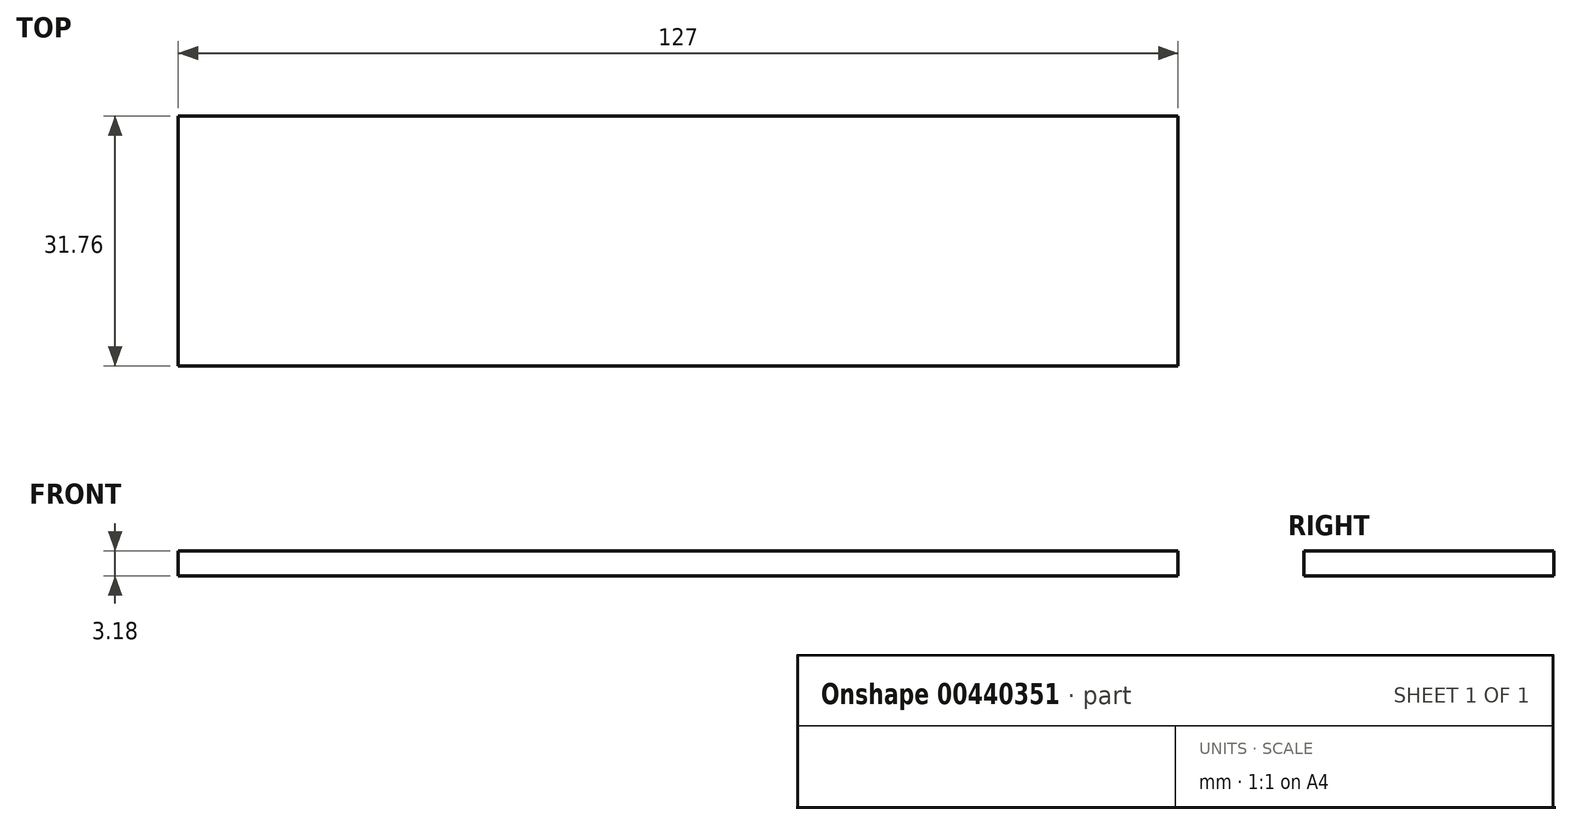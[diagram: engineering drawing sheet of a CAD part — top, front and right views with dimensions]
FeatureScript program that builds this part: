
annotation { "Feature Type Name" : "Feature", "Feature Type Description" : "" }
export const myFeature = defineFeature(function(context is Context, id is Id, definition is map)
    precondition{}
    {
        {
            var Q0;
            Q0=qCreatedBy(makeId("Top.planeOp"),FACE);
            var sketch = newSketch(context, id + "F0", { "sketchPlane" : qUnion([Q0])});
            skLineSegment(sketch, "E0.bottom", {"start": v(-63.5, 15.88) * mm, "end": v(63.5, 15.88) * mm});
            skLineSegment(sketch, "E0.top", {"start": v(-63.5, -15.87) * mm, "end": v(63.5, -15.87) * mm});
            skLineSegment(sketch, "E0.left", {"start": v(-63.5, 15.88) * mm, "end": v(-63.5, -15.87) * mm});
            skLineSegment(sketch, "E0.right", {"start": v(63.5, 15.88) * mm, "end": v(63.5, -15.87) * mm});
            skPoint(sketch, "E0.middle", {"position": v(0, 0) * mm});
            skSolve(sketch);
        }
        {
            var Q0;
            Q0=makeQuery(id+"F0.imprint","IMPRINT",FACE,{"disambiguationData":[TD([[makeQuery(id+"F0.imprint","IMPRINT",EDGE,{"derivedFrom":sQuery(id+"F0.wireOp",EDGE,"E0.bottom")}),-1.0]])]});
            extrude(context, id + "F1", {"entities" : qUnion([Q0]), "endBound" : BoundingType.SYMMETRIC, "depth" : 3.17 * mm});
        }
    });
